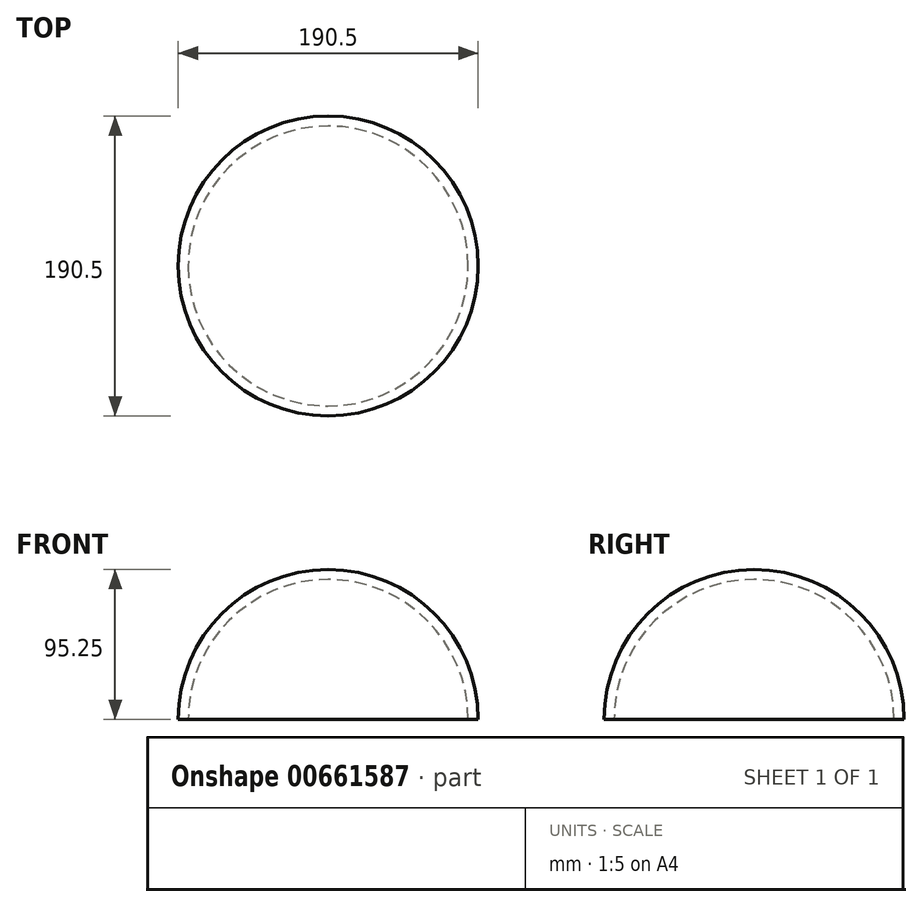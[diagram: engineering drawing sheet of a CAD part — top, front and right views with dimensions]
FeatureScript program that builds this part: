
annotation { "Feature Type Name" : "Feature", "Feature Type Description" : "" }
export const myFeature = defineFeature(function(context is Context, id is Id, definition is map)
    precondition{}
    {
        {
            var Q0;
            Q0=qCreatedBy(makeId("Top.planeOp"),FACE);
            var sketch = newSketch(context, id + "F0", { "sketchPlane" : qUnion([Q0])});
            skCircle(sketch, "E0", {"center": v(0, 0) * mm, "radius": 95.25 * mm});
            skCircle(sketch, "E1", {"center": v(0, 0) * mm, "radius": 88.9 * mm});
            skLineSegment(sketch, "E2", {"start": v(-95.25, 0) * mm, "end": v(95.25, 0) * mm});
            skSolve(sketch);
        }
        {
            var Q0;
            {var subQ0=sQuery(id+"F0.wireOp",EDGE,"E2");var subQ1=sQuery(id+"F0.wireOp",EDGE,"E0");var subQ2=makeQuery(id+"F0.imprint","INTERSECT",VERTEX,{"disambiguationData":[OD(0.0)],"derivedFrom":[subQ1,subQ0]});Q0=makeQuery(id+"F0.imprint","IMPRINT",FACE,{"disambiguationData":[TD([[makeQuery(id+"F0.imprint","IMPRINT",EDGE,{"disambiguationData":[TD([[subQ2,-1.0]])],"derivedFrom":subQ1}),1.0]])]});}
            var Q1;
            Q1=sQuery(id+"F0.wireOp",EDGE,"E2");
            revolve(context, id + "F1", {"entities" : qUnion([Q0]), "axis" : qUnion([Q1]), "revolveType" : RevolveType.ONE_DIRECTION, "angle" : 180 * degree});
        }
    });
